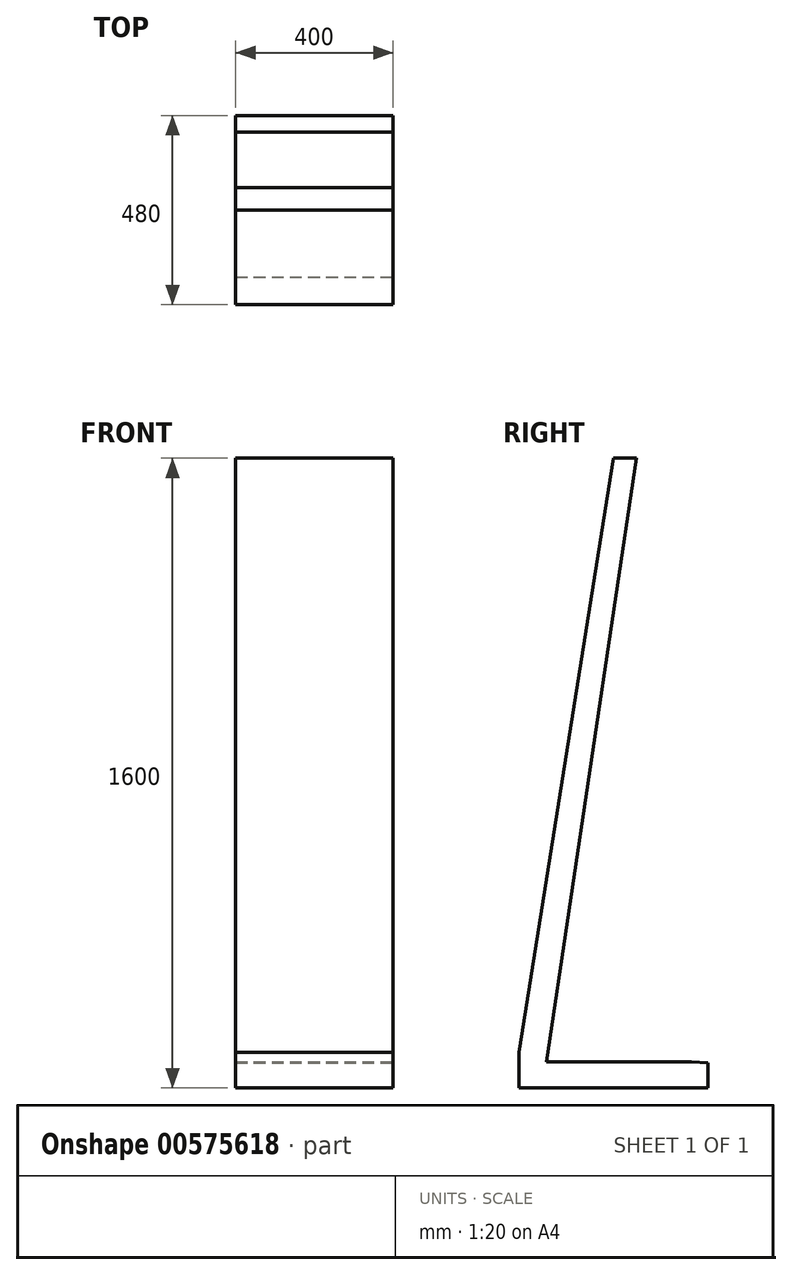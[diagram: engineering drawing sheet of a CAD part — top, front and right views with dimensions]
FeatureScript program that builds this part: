
annotation { "Feature Type Name" : "Feature", "Feature Type Description" : "" }
export const myFeature = defineFeature(function(context is Context, id is Id, definition is map)
    precondition{}
    {
        {
            var Q0;
            Q0=qCreatedBy(makeId("Top.planeOp"),FACE);
            var sketch = newSketch(context, id + "F0", { "sketchPlane" : qUnion([Q0])});
            skLineSegment(sketch, "E0.bottom", {"start": v(0, 0) * mm, "end": v(-400, 0) * mm});
            skLineSegment(sketch, "E0.top", {"start": v(0, 480) * mm, "end": v(-400, 480) * mm});
            skLineSegment(sketch, "E0.left", {"start": v(0, 0) * mm, "end": v(0, 480) * mm});
            skLineSegment(sketch, "E0.right", {"start": v(-400, 0) * mm, "end": v(-400, 480) * mm});
            skSolve(sketch);
        }
        {
            var Q0;
            Q0 = qSketchRegion(id + "F0", true);
            extrude(context, id + "F1", {"entities" : qUnion([Q0]), "depth" : 1600 * mm, "offsetDistance" : 25 * mm});
        }
        {
            var Q0;
            Q0=makeQuery(id+"F1.opExtrude","SWEPT_FACE",FACE,{"disambiguationData":[OSD([sQuery(id+"F0.wireOp",EDGE,"E0.left")])]});
            var sketch = newSketch(context, id + "F2", { "sketchPlane" : qUnion([Q0])});
            skLineSegment(sketch, "E1", {"start": v(240, 1600) * mm, "end": v(0, 89.73) * mm});
            skLineSegment(sketch, "E2", {"start": v(0, 89.73) * mm, "end": v(0, 1600) * mm});
            skLineSegment(sketch, "E3", {"start": v(0, 1600) * mm, "end": v(240, 1600) * mm});
            skLineSegment(sketch, "E4", {"start": v(438.24, 65.89) * mm, "end": v(70.06, 65.89) * mm});
            skLineSegment(sketch, "E5", {"start": v(70.06, 65.89) * mm, "end": v(297.85, 1600) * mm});
            skLineSegment(sketch, "E6", {"start": v(297.85, 1600) * mm, "end": v(480, 1600) * mm});
            skLineSegment(sketch, "E7", {"start": v(480, 1600) * mm, "end": v(480, 63.24) * mm});
            skLineSegment(sketch, "E8", {"start": v(480, 63.24) * mm, "end": v(438.24, 65.89) * mm});
            skSolve(sketch);
        }
        {
            var Q0;
            Q0 = qSketchRegion(id + "F2", true);
            extrude(context, id + "F3", {"entities" : qUnion([Q0]), "operationType" : NewBodyOperationType.REMOVE, "endBound" : BoundingType.UP_TO_NEXT, "oppositeDirection" : true, "depth" : 25 * mm, "offsetDistance" : 25 * mm});
        }
    });
